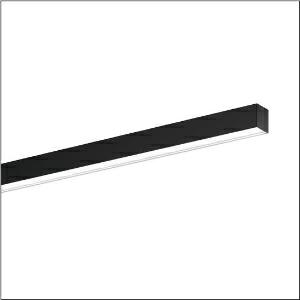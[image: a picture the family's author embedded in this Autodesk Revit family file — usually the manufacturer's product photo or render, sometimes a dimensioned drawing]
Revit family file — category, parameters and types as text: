
# Revit family: silica_r__21_51mx20dc45bb_0fdd
name_source: partatom
category: Lighting Fixtures
units: mm (PartAtom-declared; Revit-internal decimal feet)

## family parameters
Cut with Voids When Loaded = No
Host = Face
Light Source = No
Part Type = Normal
Room Calculation Point = No
Round Connector Dimension = Use Diameter
Shared = No

## types (1)
- --- (1 x LED, 6000 lm, 40.1 W, 4000K)
    Apparent Load = 40 VA
    CIE Flux Codes = 48 79 96 100 100
    Color Rendering = 80
    Color Temperature = 4000K
    Default Elevation = 1800 mm
    Description = Silica® 21, office luminaire, primary optical cover: cover, of PMMA, opal, light emission: direct distribution, primary light characteristic: symmetric, installation type: surface-mounted, LED, rated luminous flux: 6.000lm, luminous efficacy: 150lm/W, light colour: 840, colour temperature: 4000K, with terminal, 3+2-pole, max. 2.5mm², mains connection: 220..240V, AC, 50/60Hz, rated input power: 40.1W, luminaire housing, of aluminium, jet black (RAL 9005), length: 3.004mm, width: 53mm, height: 53mm, protection rating (complete): IP20, insulation class (complete): insulation class I (protective earthing), certification: CE, permissible operating ambient temperature: 0..+35°C, standard: EN 50419, packaging unit: 1 piece
    Height = 0 mm  [stored 0 ft]
    Lamp = 1 x LED
    Lamp Light Flux = 6000 lm
    Lamp Power = 40.1 W
    Lamp count = 1
    Length = 3004 mm
    Luminous efficacy = 150 lm/W
    Manufacturer = Siteco
    ModVariant = No
    Model = 51MX20DC45BB
    Mounting Place = Ceiling
    Mounting Type = Recessed
    Number of Poles = 1
    OnlyDefault = Yes
    Power Factor = 1
    Product Name = Silica® 21
    Product group = office luminaire | ceiling recessed
    ProductGroupID = 401
    Protection Class = Protection class I
    Protection Degree = IP 20
    RLX_Detail_Level = 1
    RLX_Emergency_Light_Flux = 0 lm
    RLX_Emergency_Type = 0
    RLX_Emergency_Type_DB = No
    RlxData = <blob elided: 28877 chars, md5=06508743>
    Socket = socket
    Standby Power = 0 W
    System Light Flux = 6000 lm
    System Power = 40 W
    Type Comments = factory setting: luminous flux: 100 % | dim-lin: 254 | 218 mA
    Type Image = l_1313584.jpg
    URL = http://relux.com
    VarID = @adj_066121
    Voltage = 0 V
    Weight = 0.00 kg
    Width = 53 mm

note: [stored X ft] marks values corroborated as IEEE doubles in the binary element streams (Revit-internal decimal feet)

## geometry (parser evidence)
native form markers: Blend x4, Sweep x9
no freeform markers — native parametric forms only
